# Revit family: NLRS_57_AIR_UN_wall-overflow-grill-wdvc_LT_sacs
name_source: partatom
category: Air Terminals
units: mm (PartAtom-declared; Revit-internal decimal feet)

## family parameters
Always vertical = Yes
Cut with Voids When Loaded = No
OmniClass Number = 23.75.70.21.27.11
OmniClass Title = Diffusers, Registers, and Grilles
Part Type = Normal
Room Calculation Point = No
Round Connector Dimension = Use Diameter
Shared = No
Work Plane-Based = No

## types (2) — shared parameters
Assembly Code = 57.00
Description = Wall overflow/return grill, Type WDVC
IfcDescription = Wall overflow/return grill, Type WDVC
IfcExportAs = IfcAirterminal
IfcExportType = Diffuser
Manufacturer = Solid Air Climate Solutions
Max Flow = 0 m³/h
Min Flow = 0 m³/h
Model = WDVC
NLRS_C_content_datum_uitgifte = 01-05-2024
NLRS_C_content_provider = Solid Air Climate Solutions
NLRS_C_content_versie = 2.21.01
NLRS_C_description = Wall overflow/return grill, Type WDVC
SACS_Data_Hidden = WDVC
SACS_Dummy = 1
Type Comments = Overflow version
URL = https://solid-air.nl
zero-valued in all types: Cost, Default Elevation

## per-type parameters (varying)
| type | SACS_Base_Index | SACS_Index1 | SACS_Show_Damper | SACS_X_Offset |
| WDVCOO | 0 | 0 mm  [stored 0 ft] | No | 30 mm  [stored 0.0984252 ft] |
| WDVCVO | 1 | 1 mm  [stored 0.00328084 ft] | Yes | 75 mm  [stored 0.246063 ft] |

note: [stored X ft] marks values corroborated as IEEE doubles in the binary element streams (Revit-internal decimal feet)

## geometry (parser evidence)
native form markers: Sweep x13
no freeform markers — native parametric forms only
